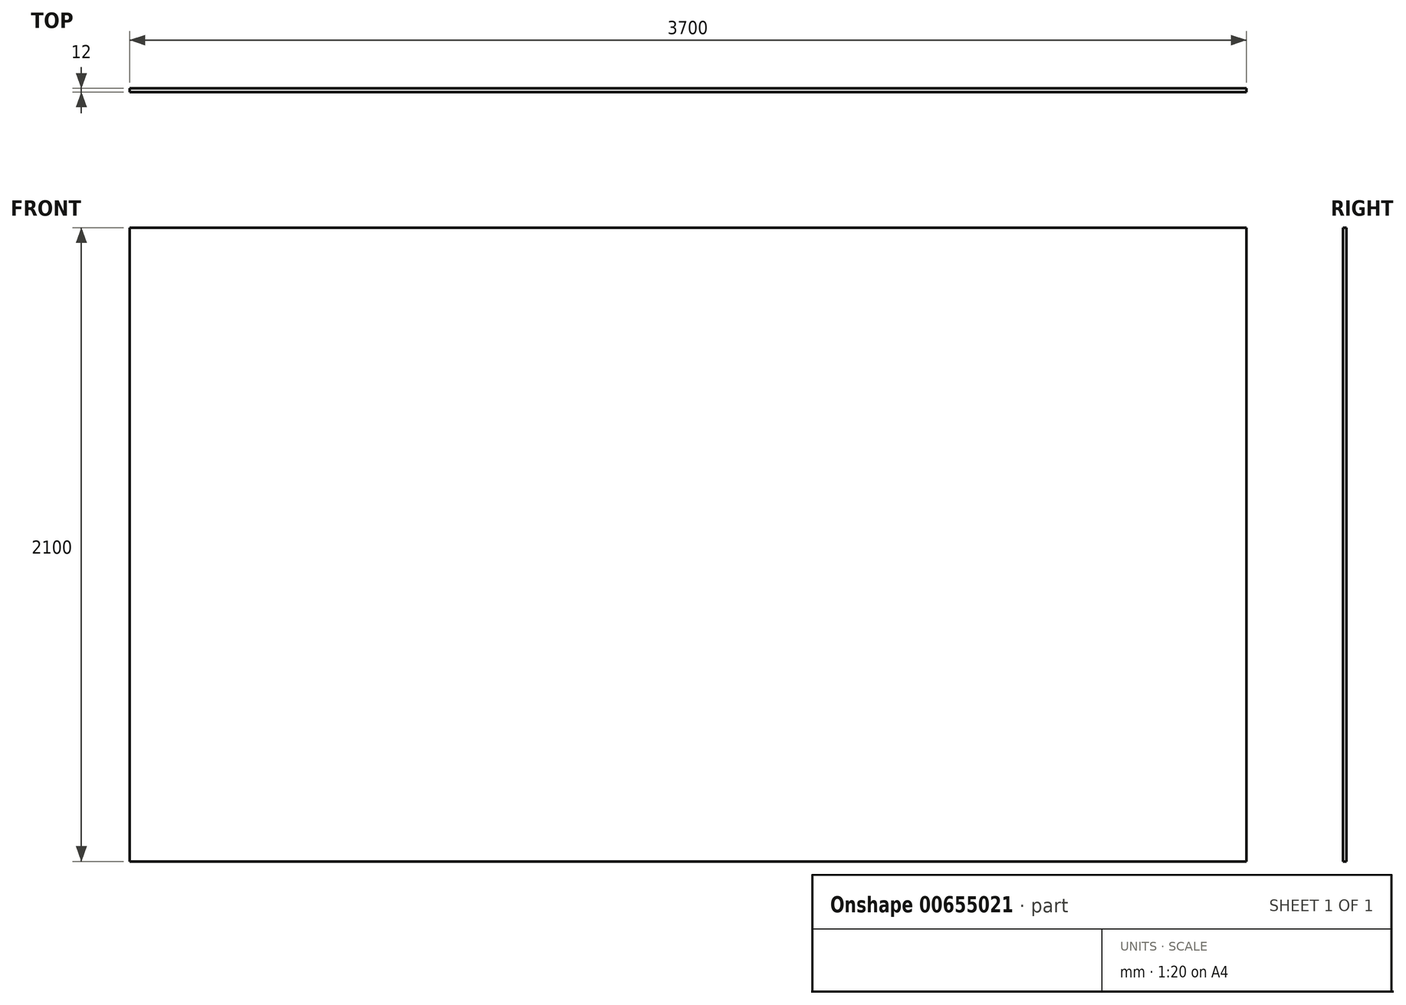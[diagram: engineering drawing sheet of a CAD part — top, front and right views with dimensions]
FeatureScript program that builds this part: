
annotation { "Feature Type Name" : "Feature", "Feature Type Description" : "" }
export const myFeature = defineFeature(function(context is Context, id is Id, definition is map)
    precondition{}
    {
        {
            var Q0;
            Q0=qCreatedBy(makeId("Front.planeOp"),FACE);
            var sketch = newSketch(context, id + "F0", { "sketchPlane" : qUnion([Q0])});
            skLineSegment(sketch, "E0.bottom", {"start": v(1850, 1050) * mm, "end": v(-1850, 1050) * mm});
            skLineSegment(sketch, "E0.top", {"start": v(1850, -1050) * mm, "end": v(-1850, -1050) * mm});
            skLineSegment(sketch, "E0.left", {"start": v(1850, 1050) * mm, "end": v(1850, -1050) * mm});
            skLineSegment(sketch, "E0.right", {"start": v(-1850, 1050) * mm, "end": v(-1850, -1050) * mm});
            skPoint(sketch, "E0.middle", {"position": v(0, 0) * mm});
            skSolve(sketch);
        }
        {
            var Q0;
            Q0 = qSketchRegion(id + "F0", true);
            extrude(context, id + "F1", {"entities" : qUnion([Q0]), "depth" : 12 * mm, "offsetDistance" : 25.4 * mm});
        }
    });
